# Revit family: 303_R402PX_
name_source: partatom
category: Pipe Accessories
revit_build: Autodesk Revit 2018 (Build: 20170223_1515(x64)
units: mm (PartAtom-declared; Revit-internal decimal feet)

## family parameters
Always vertical = Yes
Cut with Voids When Loaded = No
Part Type = Valve - Breaks Into
Round Connector Dimension = Use Diameter
Shared = No
Work Plane-Based = No

## types (3) — shared parameters
CAT0 = Yes
D3 = 13 mm  [stored 0.0426509 ft]
Description = Straight valve with precision adjustment numberscale and protection cap
J12 = 5 mm  [stored 0.0164042 ft]
J12__ve = -5 mm  [stored -0.0164042 ft]
J13 = 5 mm  [stored 0.0164042 ft]
L2D_Min = 3048 mm  [stored 10 ft]
L6 = 5 mm  [stored 0.0164042 ft]
L6__ve = -5 mm  [stored -0.0164042 ft]
M1 = 12 mm  [stored 0.0393701 ft]
Manufacturer = Giacomini
QmdConnectorList = 301;D;302;D1
URL = http://www.giacomini.com
magiPartTypeId = 303
magiProductFamilyId = R402PX*
zero-valued in all types: MC_Default_elevation

## per-type parameters (varying)
- R402PX032: CenSd_K2_6=10 mm  [stored 0.0328084 ft]; CenSd_W2_6=12 mm  [stored 0.0393701 ft]; D=10 mm; D1=10 mm; G3=10 mm  [stored 0.0328084 ft]; J5=30 mm  [stored 0.0984252 ft]; K2=11 mm  [stored 0.0360892 ft]; K3=9 mm  [stored 0.0295276 ft]; L2=10 mm  [stored 0.0328084 ft]; L2D=68 mm; L4=7 mm  [stored 0.0229659 ft]; L5=10 mm  [stored 0.0328084 ft]; L61=2 mm  [stored 0.00656168 ft]; L61__ve=-2 mm  [stored -0.00656168 ft]; LC=56 mm  [stored 0.183727 ft]; LC1=32 mm  [stored 0.104987 ft]; LC2=53 mm; LX=32 mm  [stored 0.104987 ft]; R1=8 mm  [stored 0.0262467 ft]; W2=14 mm  [stored 0.0459318 ft]; W2D=10 mm  [stored 0.0328084 ft]; W4=8 mm  [stored 0.0262467 ft]; X11=15 mm  [stored 0.0492126 ft]; Z1=10 mm  [stored 0.0328084 ft]; Z2=11 mm  [stored 0.0360892 ft]
- R402PX034: CenSd_K2_6=14 mm  [stored 0.0459318 ft]; CenSd_W2_6=16 mm  [stored 0.0524934 ft]; D=20 mm; D1=20 mm; G3=15 mm  [stored 0.0492126 ft]; J5=33 mm; K2=16 mm  [stored 0.0524934 ft]; K3=13 mm  [stored 0.0426509 ft]; L2=9 mm  [stored 0.0295276 ft]; L2D=61 mm; L4=7 mm  [stored 0.0229659 ft]; L5=9 mm  [stored 0.0295276 ft]; L61=2 mm  [stored 0.00656168 ft]; L61__ve=-2 mm  [stored -0.00656168 ft]; LC=56 mm  [stored 0.183727 ft]; LC1=31 mm; LC2=51 mm; LX=31 mm; R1=13 mm  [stored 0.0426509 ft]; W2=19 mm  [stored 0.062336 ft]; W2D=20 mm  [stored 0.0656168 ft]; W4=11 mm  [stored 0.0360892 ft]; X11=14 mm  [stored 0.0459318 ft]; Z1=14 mm  [stored 0.0459318 ft]; Z2=9 mm  [stored 0.0295276 ft]
- R402PX033: CenSd_K2_6=12 mm  [stored 0.0393701 ft]; CenSd_W2_6=13 mm  [stored 0.0426509 ft]; D=15 mm; D1=15 mm; G3=12 mm  [stored 0.0393701 ft]; J5=30 mm  [stored 0.0984252 ft]; K2=14 mm  [stored 0.0459318 ft]; K3=11 mm  [stored 0.0360892 ft]; L2=11 mm  [stored 0.0360892 ft]; L2D=69 mm; L4=8 mm  [stored 0.0262467 ft]; L5=11 mm  [stored 0.0360892 ft]; L61=3 mm  [stored 0.00984252 ft]; L61__ve=-3 mm; LC=60 mm; LC1=35 mm; LC2=58 mm; LX=36 mm; R1=11 mm  [stored 0.0360892 ft]; W2=15 mm  [stored 0.0492126 ft]; W2D=15 mm  [stored 0.0492126 ft]; W4=9 mm  [stored 0.0295276 ft]; X11=16 mm  [stored 0.0524934 ft]; Z1=11 mm  [stored 0.0360892 ft]; Z2=10 mm  [stored 0.0328084 ft]

note: column(s) folded — value = type name in every type: magiProductCode, magiProductId

note: [stored X ft] marks values corroborated as IEEE doubles in the binary element streams (Revit-internal decimal feet)

## geometry (parser evidence)
native form markers: Sweep x1
no freeform markers — native parametric forms only
